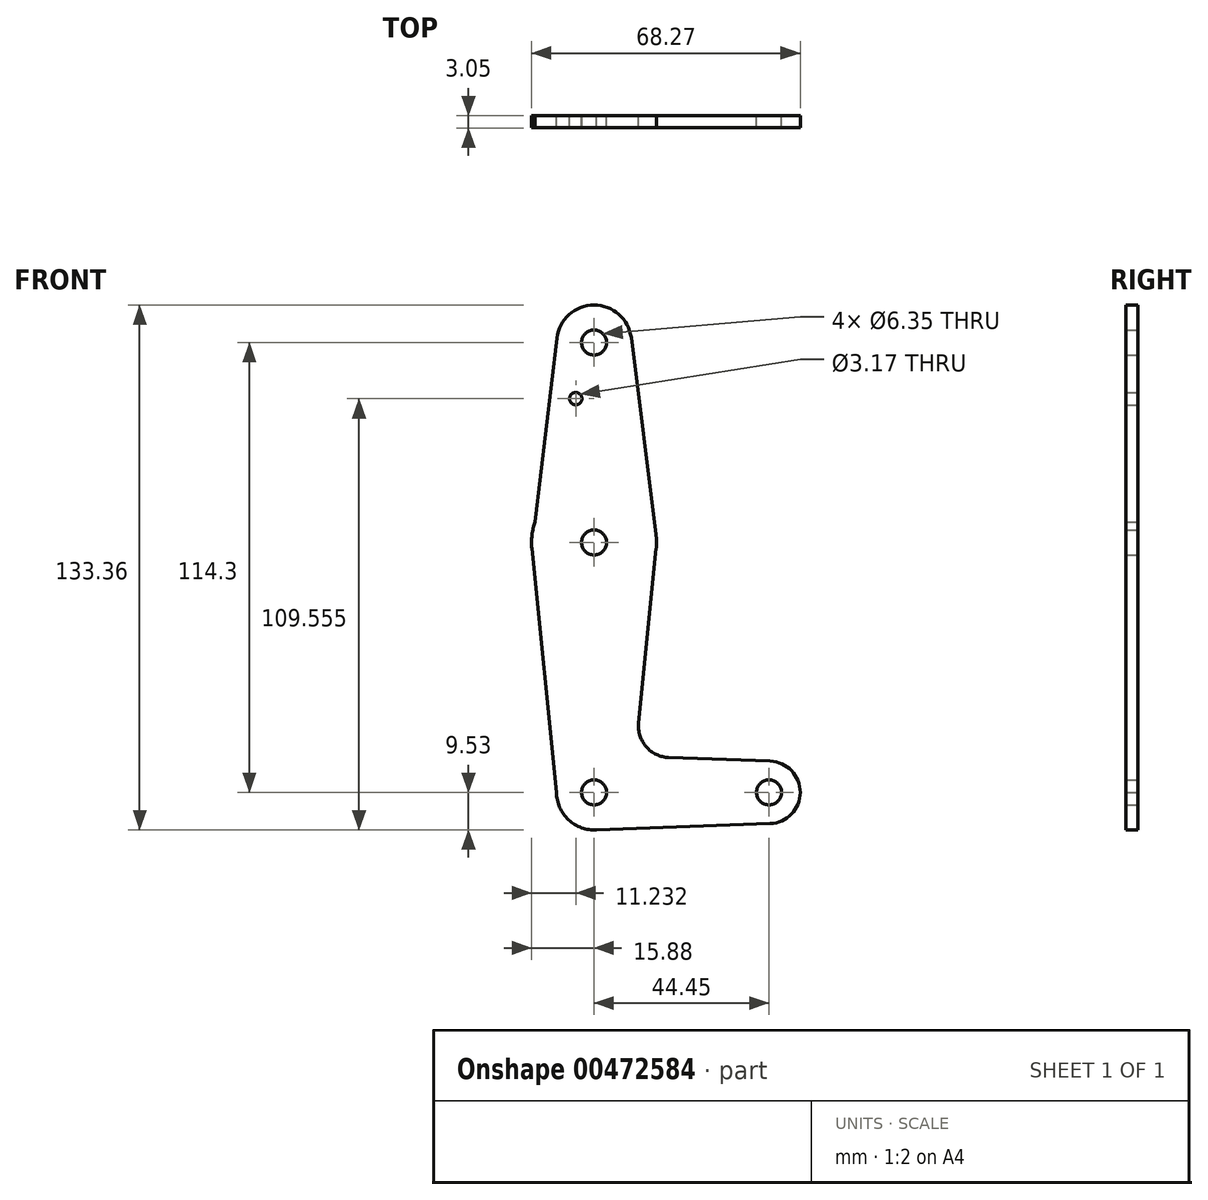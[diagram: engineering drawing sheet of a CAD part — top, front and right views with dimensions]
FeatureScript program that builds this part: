
annotation { "Feature Type Name" : "Feature", "Feature Type Description" : "" }
export const myFeature = defineFeature(function(context is Context, id is Id, definition is map)
    precondition{}
    {
        {
            var Q0;
            Q0=qCreatedBy(makeId("Front.planeOp"),FACE);
            var sketch = newSketch(context, id + "F0", { "sketchPlane" : qUnion([Q0])});
            skLineSegment(sketch, "E0", {"start": v(0, 0) * mm, "end": v(0, 114.3) * mm});
            skLineSegment(sketch, "E1", {"start": v(0, 0) * mm, "end": v(44.45, 0) * mm});
            skCircle(sketch, "E2", {"center": v(0, 114.3) * mm, "radius": 9.53 * mm});
            skCircle(sketch, "E3", {"center": v(0, 0) * mm, "radius": 9.53 * mm});
            skCircle(sketch, "E4", {"center": v(44.45, 0) * mm, "radius": 7.94 * mm});
            skCircle(sketch, "E5", {"center": v(0, 63.5) * mm, "radius": 15.88 * mm});
            skLineSegment(sketch, "E6", {"start": v(-15.8, 61.9) * mm, "end": v(-9.46, 115.42) * mm});
            skLineSegment(sketch, "E7", {"start": v(9.45, 115.5) * mm, "end": v(15.75, 65.48) * mm});
            skLineSegment(sketch, "E8", {"start": v(15.8, 61.91) * mm, "end": v(11.34, 17.59) * mm});
            skLineSegment(sketch, "E9", {"start": v(-9.53, 0) * mm, "end": v(-15.8, 61.9) * mm});
            skLineSegment(sketch, "E10", {"start": v(18.97, 8.85) * mm, "end": v(44.73, 7.93) * mm});
            skArc(sketch, "E11", {"start": v(16.08, 24.09) * mm, "mid": v(12.63, 12.4) * mm, "end": v(24.73, 11.04) * mm});
            skCircle(sketch, "E12", {"center": v(0, 114.3) * mm, "radius": 3.18 * mm});
            skCircle(sketch, "E13", {"center": v(0, 63.5) * mm, "radius": 3.18 * mm});
            skCircle(sketch, "E14", {"center": v(0, 0) * mm, "radius": 3.18 * mm});
            skCircle(sketch, "E15", {"center": v(44.45, 0) * mm, "radius": 3.18 * mm});
            skCircle(sketch, "E16", {"center": v(-4.65, 100.03) * mm, "radius": 1.59 * mm});
            skArc(sketch, "E17.filletArc", {"start": v(11.34, 17.59) * mm, "mid": v(13.26, 11.57) * mm, "end": v(18.97, 8.85) * mm});
            skLineSegment(sketch, "E18", {"start": v(0, -9.53) * mm, "end": v(44.73, -7.93) * mm});
            skSolve(sketch);
        }
        {
            var Q0;
            Q0 = qSketchRegion(id + "F0", true);
            var Q1;
            {var subQ0=sQuery(id+"F0.wireOp",EDGE,"E14");var subQ1=sQuery(id+"F0.wireOp",EDGE,"E0");var subQ2=makeQuery(id+"F0.imprint","INTERSECT",VERTEX,{"derivedFrom":[subQ1,subQ0]});Q1=makeQuery(id+"F0.imprint","IMPRINT",FACE,{"disambiguationData":[TD([[makeQuery(id+"F0.imprint","IMPRINT",EDGE,{"disambiguationData":[TD([[subQ2,-1.0]])],"derivedFrom":subQ1}),-1.0]])]});}
            extrude(context, id + "F1", {"entities" : qUnion([Q0, Q1]), "depth" : 3.05 * mm});
        }
    });
